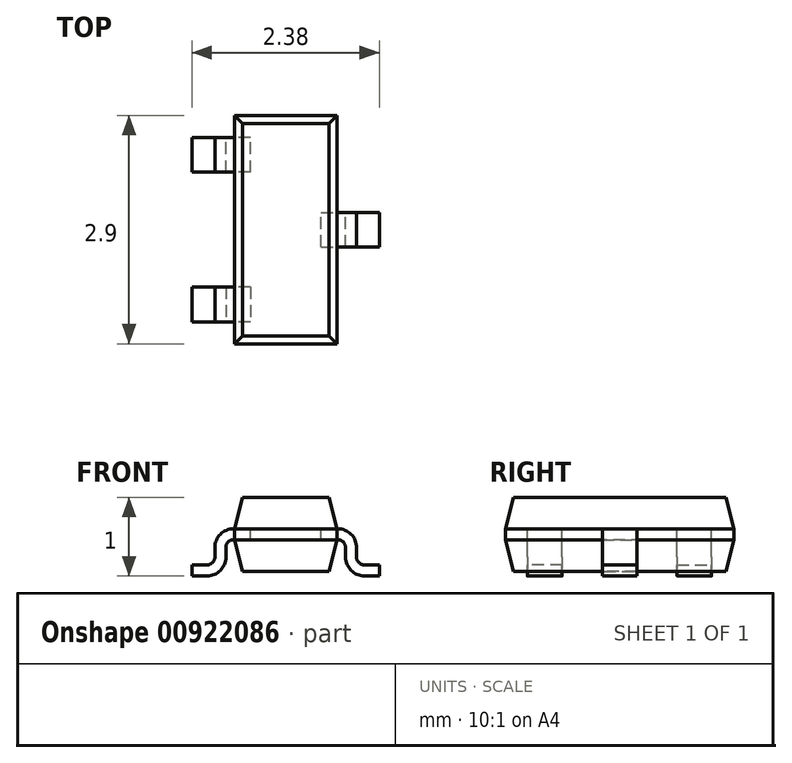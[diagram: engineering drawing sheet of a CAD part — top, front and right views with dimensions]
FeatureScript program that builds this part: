
annotation { "Feature Type Name" : "Feature", "Feature Type Description" : "" }
export const myFeature = defineFeature(function(context is Context, id is Id, definition is map)
    precondition{}
    {
        {
            var Q0;
            Q0=qCreatedBy(makeId("Front.planeOp"),FACE);
            var sketch = newSketch(context, id + "F0", { "sketchPlane" : qUnion([Q0])});
            skLineSegment(sketch, "E0.bottom", {"start": v(-0.65, 0.47) * mm, "end": v(0.65, 0.47) * mm});
            skLineSegment(sketch, "E0.top", {"start": v(-0.65, -0.47) * mm, "end": v(0.65, -0.47) * mm});
            skLineSegment(sketch, "E0.left", {"start": v(-0.65, 0.47) * mm, "end": v(-0.65, -0.47) * mm});
            skLineSegment(sketch, "E0.right", {"start": v(0.65, 0.47) * mm, "end": v(0.65, -0.47) * mm});
            skPoint(sketch, "E0.middle", {"position": v(0, 0) * mm});
            skLineSegment(sketch, "E1", {"start": v(0.45, 0) * mm, "end": v(0.45, 0.07) * mm});
            skPoint(sketch, "E1.startSnap0", {"position": v(0.65, 0) * mm});
            skLineSegment(sketch, "E2", {"start": v(0.45, 0.07) * mm, "end": v(0.65, 0.07) * mm});
            skLineSegment(sketch, "E3", {"start": v(0.45, 0) * mm, "end": v(0.45, -0.07) * mm});
            skLineSegment(sketch, "E4", {"start": v(0.45, -0.07) * mm, "end": v(0.65, -0.07) * mm});
            skLineSegment(sketch, "E5", {"start": v(1.2, -0.53) * mm, "end": v(1.2, -0.39) * mm});
            skLineSegment(sketch, "E6", {"start": v(1.2, -0.39) * mm, "end": v(1, -0.39) * mm});
            skLineSegment(sketch, "E7", {"start": v(1.2, -0.53) * mm, "end": v(1, -0.53) * mm});
            skLineSegment(sketch, "E8", {"start": v(0.76, -0.3) * mm, "end": v(0.76, -0.17) * mm});
            skLineSegment(sketch, "E9", {"start": v(0.66, -0.07) * mm, "end": v(0.65, -0.07) * mm});
            skLineSegment(sketch, "E10", {"start": v(0.9, -0.3) * mm, "end": v(0.9, -0.17) * mm});
            skLineSegment(sketch, "E11", {"start": v(0.66, 0.07) * mm, "end": v(0.65, 0.07) * mm});
            skPoint(sketch, "E12.visualSharp", {"position": v(0.9, -0.39) * mm});
            skArc(sketch, "E12.filletArc", {"start": v(0.9, -0.3) * mm, "mid": v(0.93, -0.36) * mm, "end": v(1, -0.4) * mm});
            skPoint(sketch, "E13.visualSharp", {"position": v(0.76, -0.53) * mm});
            skArc(sketch, "E13.filletArc", {"start": v(0.76, -0.3) * mm, "mid": v(0.83, -0.46) * mm, "end": v(1, -0.53) * mm});
            skPoint(sketch, "E14.visualSharp", {"position": v(0.76, -0.07) * mm});
            skArc(sketch, "E14.filletArc", {"start": v(0.76, -0.17) * mm, "mid": v(0.73, -0.1) * mm, "end": v(0.66, -0.07) * mm});
            skPoint(sketch, "E15.visualSharp", {"position": v(0.9, 0.07) * mm});
            skArc(sketch, "E15.filletArc", {"start": v(0.9, -0.17) * mm, "mid": v(0.83, 0) * mm, "end": v(0.66, 0.07) * mm});
            skSolve(sketch);
        }
        {
            var Q0;
            Q0=makeQuery(id+"F0.imprint","IMPRINT",FACE,{"disambiguationData":[TD([[makeQuery(id+"F0.imprint","IMPRINT",EDGE,{"derivedFrom":sQuery(id+"F0.wireOp",EDGE,"E1")}),-1.0]])]});
            var Q1;
            Q1=makeQuery(id+"F0.imprint","IMPRINT",FACE,{"disambiguationData":[TD([[makeQuery(id+"F0.imprint","IMPRINT",EDGE,{"derivedFrom":sQuery(id+"F0.wireOp",EDGE,"E5")}),1.0]])]});
            extrude(context, id + "F1", {"entities" : qUnion([Q0, Q1]), "endBound" : BoundingType.SYMMETRIC, "depth" : 0.44 * mm, "offsetDistance" : 25 * mm});
        }
        {
            var Q0;
            {var subQ1=sQuery(id+"F0.wireOp",EDGE,"E0.bottom");Q0=makeQuery(id+"F0.imprint","IMPRINT",FACE,{"disambiguationData":[TD([[makeQuery(id+"F0.imprint","IMPRINT",EDGE,{"derivedFrom":subQ1}),-1.0]])]});}
            var Q1;
            Q1=makeQuery(id+"F0.imprint","IMPRINT",FACE,{"disambiguationData":[TD([[makeQuery(id+"F0.imprint","IMPRINT",EDGE,{"derivedFrom":sQuery(id+"F0.wireOp",EDGE,"E1")}),-1.0]])]});
            extrude(context, id + "F2", {"entities" : qUnion([Q0, Q1]), "endBound" : BoundingType.SYMMETRIC, "depth" : 2.9 * mm, "offsetDistance" : 25 * mm});
        }
        {
            var Q0;
            Q0=makeQuery(id+"F1.opExtrude","SWEPT_BODY",BODY,{"disambiguationData":[OSD([sQuery(id+"F0.wireOp",EDGE,"E1"),sQuery(id+"F0.wireOp",EDGE,"E2"),sQuery(id+"F0.wireOp",EDGE,"E3"),sQuery(id+"F0.wireOp",EDGE,"E4"),sQuery(id+"F0.wireOp",EDGE,"E5"),sQuery(id+"F0.wireOp",EDGE,"E6"),sQuery(id+"F0.wireOp",EDGE,"E7"),sQuery(id+"F0.wireOp",EDGE,"E8"),sQuery(id+"F0.wireOp",EDGE,"E9"),sQuery(id+"F0.wireOp",EDGE,"E10"),sQuery(id+"F0.wireOp",EDGE,"E11"),sQuery(id+"F0.wireOp",EDGE,"E12.filletArc"),sQuery(id+"F0.wireOp",EDGE,"E13.filletArc"),sQuery(id+"F0.wireOp",EDGE,"E14.filletArc"),sQuery(id+"F0.wireOp",EDGE,"E15.filletArc")])]});
            var Q1;
            Q1=qCreatedBy(makeId("Right.planeOp"),FACE);
            mirror(context, id + "F3", {"entities" : qUnion([Q0]), "mirrorPlane" : qUnion([Q1])});
        }
        {
            var Q0;
            Q0=makeQuery(id+"F2.opExtrude","SWEPT_FACE",FACE,{"disambiguationData":[OSD([sQuery(id+"F0.wireOp",EDGE,"E0.bottom")])]});
            chamfer(context, id + "F4", {"entities" : qUnion([Q0]), "chamferType" : ChamferType.TWO_OFFSETS, "width1" : 0.4 * mm, "oppositeDirection" : false, "width2" : 0.1 * mm, "tangentPropagation" : true});
        }
        {
            var Q0;
            Q0=makeQuery(id+"F2.opExtrude","SWEPT_FACE",FACE,{"disambiguationData":[OSD([sQuery(id+"F0.wireOp",EDGE,"E0.top")])]});
            chamfer(context, id + "F5", {"entities" : qUnion([Q0]), "chamferType" : ChamferType.TWO_OFFSETS, "width1" : 0.1 * mm, "oppositeDirection" : false, "width2" : 0.4 * mm, "tangentPropagation" : true});
        }
        {
            var Q0;
            Q0=makeQuery(id+"F3.opPattern","COPY",BODY,{"derivedFrom":makeQuery(id+"F1.opExtrude","SWEPT_BODY",BODY,{"disambiguationData":[OSD([sQuery(id+"F0.wireOp",EDGE,"E1"),sQuery(id+"F0.wireOp",EDGE,"E2"),sQuery(id+"F0.wireOp",EDGE,"E3"),sQuery(id+"F0.wireOp",EDGE,"E4"),sQuery(id+"F0.wireOp",EDGE,"E5"),sQuery(id+"F0.wireOp",EDGE,"E6"),sQuery(id+"F0.wireOp",EDGE,"E7"),sQuery(id+"F0.wireOp",EDGE,"E8"),sQuery(id+"F0.wireOp",EDGE,"E9"),sQuery(id+"F0.wireOp",EDGE,"E10"),sQuery(id+"F0.wireOp",EDGE,"E11"),sQuery(id+"F0.wireOp",EDGE,"E12.filletArc"),sQuery(id+"F0.wireOp",EDGE,"E13.filletArc"),sQuery(id+"F0.wireOp",EDGE,"E14.filletArc"),sQuery(id+"F0.wireOp",EDGE,"E15.filletArc")])]}),"instanceName":"1"});
            transform(context, id + "F6", {"entities" : qUnion([Q0]), "transformType" : TransformType.TRANSLATION_3D, "dx" : 0 * mm, "dy" : (1.9 / 2) * mm, "dz" : 0 * mm, "makeCopy" : false});
        }
        {
            var Q0;
            Q0=makeQuery(id+"F3.opPattern","COPY",BODY,{"derivedFrom":makeQuery(id+"F1.opExtrude","SWEPT_BODY",BODY,{"disambiguationData":[OSD([sQuery(id+"F0.wireOp",EDGE,"E1"),sQuery(id+"F0.wireOp",EDGE,"E2"),sQuery(id+"F0.wireOp",EDGE,"E3"),sQuery(id+"F0.wireOp",EDGE,"E4"),sQuery(id+"F0.wireOp",EDGE,"E5"),sQuery(id+"F0.wireOp",EDGE,"E6"),sQuery(id+"F0.wireOp",EDGE,"E7"),sQuery(id+"F0.wireOp",EDGE,"E8"),sQuery(id+"F0.wireOp",EDGE,"E9"),sQuery(id+"F0.wireOp",EDGE,"E10"),sQuery(id+"F0.wireOp",EDGE,"E11"),sQuery(id+"F0.wireOp",EDGE,"E12.filletArc"),sQuery(id+"F0.wireOp",EDGE,"E13.filletArc"),sQuery(id+"F0.wireOp",EDGE,"E14.filletArc"),sQuery(id+"F0.wireOp",EDGE,"E15.filletArc")])]}),"instanceName":"1"});
            var Q1;
            Q1=qCreatedBy(makeId("Front.planeOp"),FACE);
            mirror(context, id + "F7", {"entities" : qUnion([Q0]), "mirrorPlane" : qUnion([Q1])});
        }
    });
